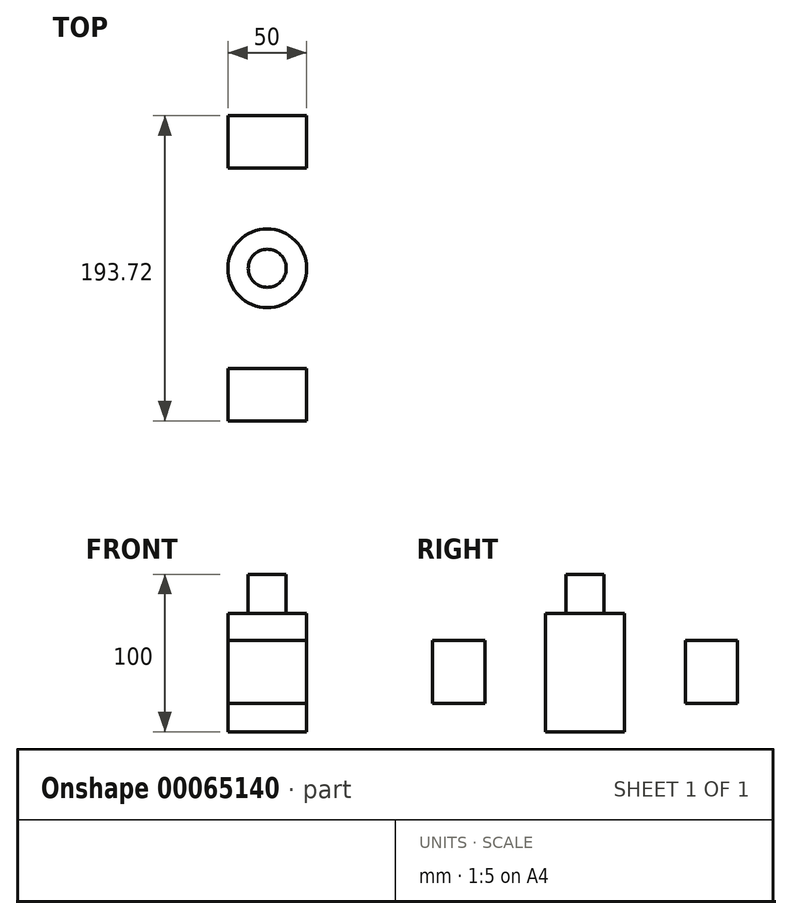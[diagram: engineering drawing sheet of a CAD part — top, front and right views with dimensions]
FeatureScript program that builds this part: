
annotation { "Feature Type Name" : "Feature", "Feature Type Description" : "" }
export const myFeature = defineFeature(function(context is Context, id is Id, definition is map)
    precondition{}
    {
        {
            var Q0;
            Q0=qCreatedBy(makeId("Top.planeOp"),FACE);
            var sketch = newSketch(context, id + "F0", { "sketchPlane" : qUnion([Q0])});
            skCircle(sketch, "E0", {"center": v(0, 0) * mm, "radius": 25 * mm});
            skSolve(sketch);
        }
        {
            var Q0;
            Q0=makeQuery(id+"F0.imprint","IMPRINT",FACE,{"disambiguationData":[TD([[makeQuery(id+"F0.imprint","IMPRINT",EDGE,{"derivedFrom":sQuery(id+"F0.wireOp",EDGE,"E0")}),1.0]])]});
            extrude(context, id + "F1", {"entities" : qUnion([Q0]), "depth" : 100 * mm});
        }
        {
            var Q0;
            Q0=makeQuery(id+"F1.opExtrude","CAP_FACE",FACE,{"disambiguationData":[OSD([sQuery(id+"F0.wireOp",EDGE,"E0")])],"isStart":false});
            var sketch = newSketch(context, id + "F2", { "sketchPlane" : qUnion([Q0])});
            skCircle(sketch, "E1", {"center": v(0, 0) * mm, "radius": 12.08 * mm});
            skSolve(sketch);
        }
        {
            var Q0;
            Q0=makeQuery(id+"F2.imprint","IMPRINT",FACE,{"disambiguationData":[TD([[makeQuery(id+"F2.imprint","IMPRINT",EDGE,{"derivedFrom":sQuery(id+"F2.wireOp",EDGE,"E1")}),-1.0]])]});
            extrude(context, id + "F3", {"entities" : qUnion([Q0]), "operationType" : NewBodyOperationType.REMOVE, "oppositeDirection" : true, "depth" : 25 * mm});
        }
        {
            var Q0;
            Q0=qCreatedBy(makeId("Right.planeOp"),FACE);
            var sketch = newSketch(context, id + "F4", { "sketchPlane" : qUnion([Q0])});
            skLineSegment(sketch, "E2.bottom", {"start": v(-96.86, 57.87) * mm, "end": v(-63.7, 57.87) * mm});
            skLineSegment(sketch, "E2.top", {"start": v(-96.86, 17.92) * mm, "end": v(-63.7, 17.92) * mm});
            skLineSegment(sketch, "E2.left", {"start": v(-96.86, 57.87) * mm, "end": v(-96.86, 17.92) * mm});
            skLineSegment(sketch, "E2.right", {"start": v(-63.7, 57.87) * mm, "end": v(-63.7, 17.92) * mm});
            skSolve(sketch);
        }
        {
            var Q0;
            Q0=makeQuery(id+"F4.imprint","IMPRINT",FACE,{"disambiguationData":[TD([[makeQuery(id+"F4.imprint","IMPRINT",EDGE,{"derivedFrom":sQuery(id+"F4.wireOp",EDGE,"E2.bottom")}),-1.0]])]});
            extrude(context, id + "F5", {"entities" : qUnion([Q0]), "endBound" : BoundingType.SYMMETRIC, "depth" : 50 * mm});
        }
        {
            var Q0;
            Q0=makeQuery(id+"F5.opExtrude","SWEPT_BODY",BODY,{"disambiguationData":[OSD([sQuery(id+"F4.wireOp",EDGE,"E2.bottom"),sQuery(id+"F4.wireOp",EDGE,"E2.top"),sQuery(id+"F4.wireOp",EDGE,"E2.left"),sQuery(id+"F4.wireOp",EDGE,"E2.right")])]});
            var Q1;
            Q1=qCreatedBy(makeId("Front.planeOp"),FACE);
            mirror(context, id + "F6", {"entities" : qUnion([Q0]), "mirrorPlane" : qUnion([Q1])});
        }
    });
